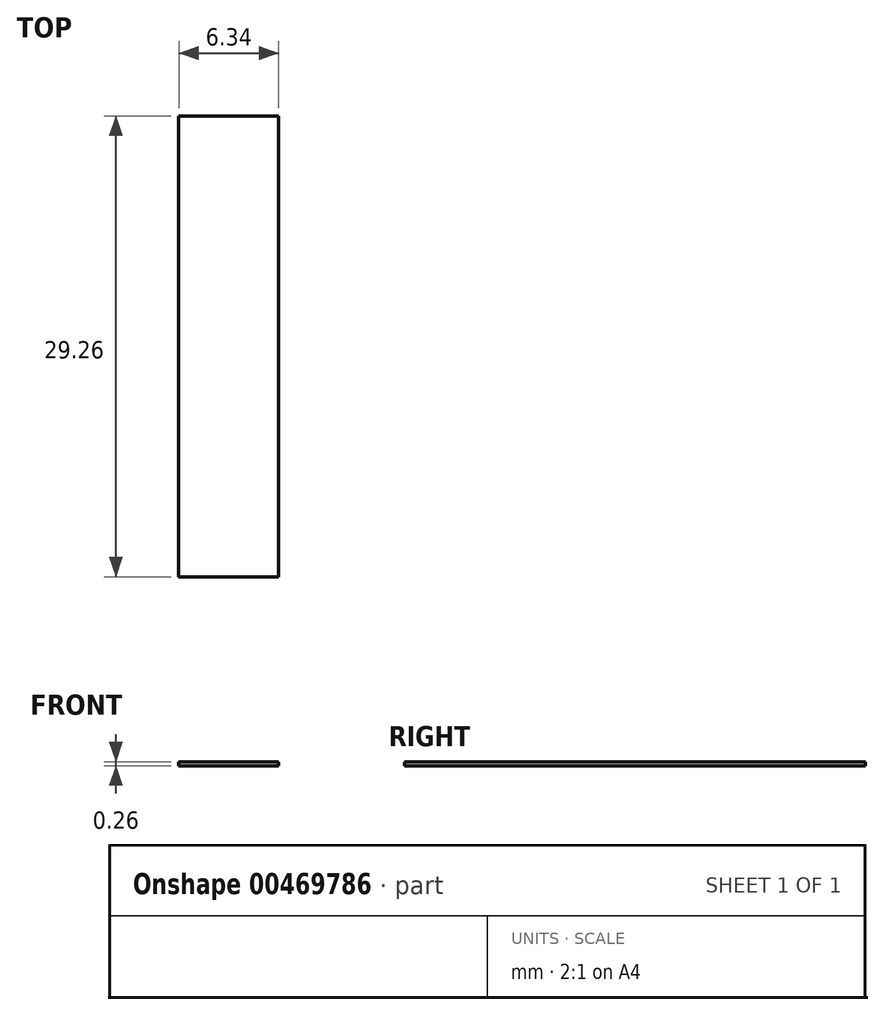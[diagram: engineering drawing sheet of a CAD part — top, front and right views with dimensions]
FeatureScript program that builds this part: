
annotation { "Feature Type Name" : "Feature", "Feature Type Description" : "" }
export const myFeature = defineFeature(function(context is Context, id is Id, definition is map)
    precondition{}
    {
        {
            var Q0;
            Q0=qCreatedBy(makeId("Front.planeOp"),FACE);
            var sketch = newSketch(context, id + "F0", { "sketchPlane" : qUnion([Q0])});
            skLineSegment(sketch, "E0.bottom", {"start": v(3.18, -0.13) * mm, "end": v(-3.17, -0.13) * mm});
            skLineSegment(sketch, "E0.top", {"start": v(3.17, 0.13) * mm, "end": v(-3.17, 0.13) * mm});
            skLineSegment(sketch, "E0.left", {"start": v(3.18, -0.13) * mm, "end": v(3.18, 0.13) * mm});
            skLineSegment(sketch, "E0.right", {"start": v(-3.17, -0.13) * mm, "end": v(-3.17, 0.13) * mm});
            skPoint(sketch, "E0.middle", {"position": v(0, 0) * mm});
            skSolve(sketch);
        }
        {
            var Q0;
            Q0 = qSketchRegion(id + "F0", true);
            extrude(context, id + "F1", {"entities" : qUnion([Q0]), "depth" : 29.26 * mm});
        }
    });
